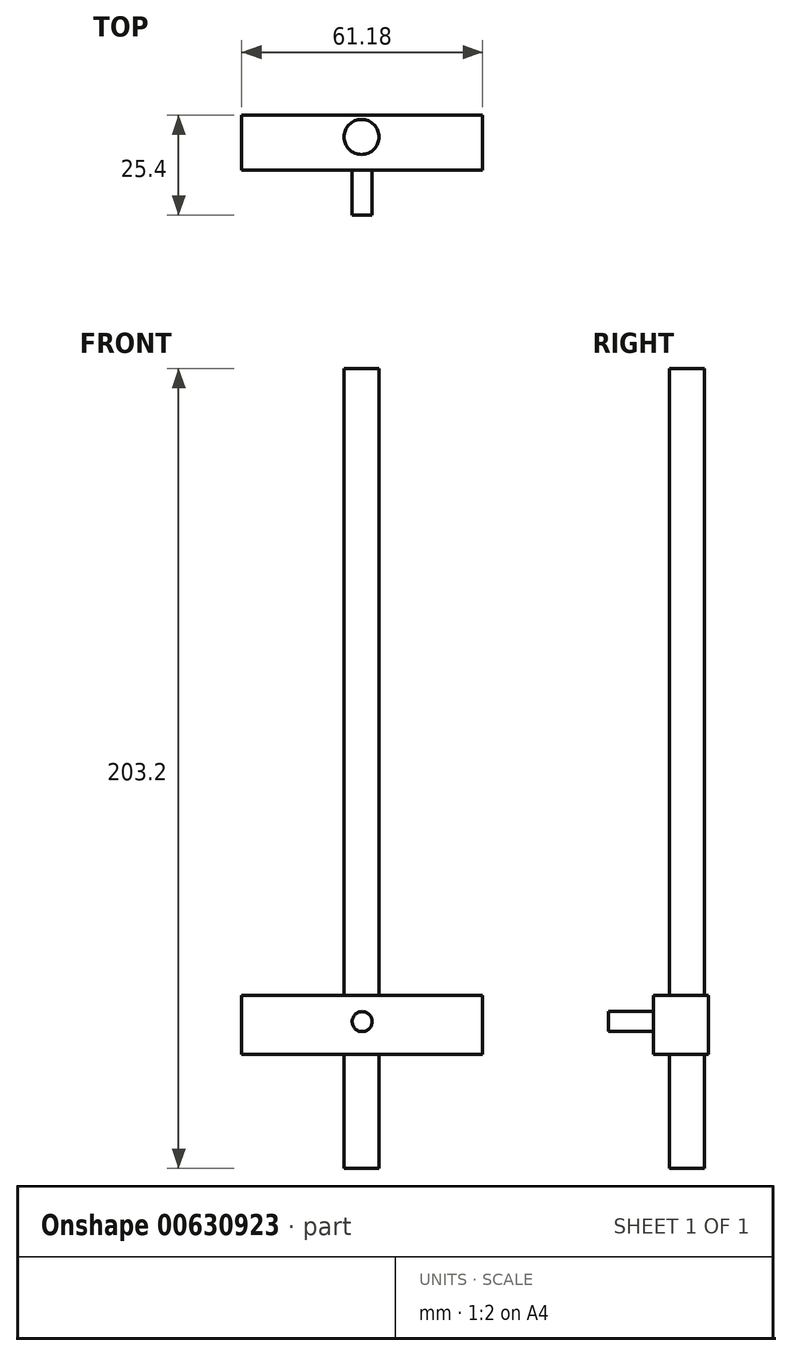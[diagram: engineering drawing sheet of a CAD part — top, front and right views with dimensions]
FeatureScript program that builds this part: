
annotation { "Feature Type Name" : "Feature", "Feature Type Description" : "" }
export const myFeature = defineFeature(function(context is Context, id is Id, definition is map)
    precondition{}
    {
        {
            var Q0;
            Q0=qCreatedBy(makeId("Top.planeOp"),FACE);
            var sketch = newSketch(context, id + "F0", { "sketchPlane" : qUnion([Q0])});
            skCircle(sketch, "E0", {"center": v(-34.22, 8.44) * mm, "radius": 4.45 * mm});
            skSolve(sketch);
        }
        {
            var Q0;
            Q0 = qSketchRegion(id + "F0", true);
            extrude(context, id + "F1", {"entities" : qUnion([Q0]), "oppositeDirection" : true, "depth" : 203.2 * mm, "offsetDistance" : 25.4 * mm});
        }
        {
            var Q0;
            Q0=qCreatedBy(makeId("Front.planeOp"),FACE);
            var sketch = newSketch(context, id + "F2", { "sketchPlane" : qUnion([Q0])});
            skLineSegment(sketch, "E1.bottom", {"start": v(-3.48, -159.3) * mm, "end": v(-64.66, -159.3) * mm});
            skLineSegment(sketch, "E1.top", {"start": v(-3.48, -174.25) * mm, "end": v(-64.66, -174.25) * mm});
            skLineSegment(sketch, "E1.left", {"start": v(-3.48, -159.3) * mm, "end": v(-3.48, -174.25) * mm});
            skLineSegment(sketch, "E1.right", {"start": v(-64.66, -159.3) * mm, "end": v(-64.66, -174.25) * mm});
            skCircle(sketch, "E2", {"center": v(-34.07, -165.91) * mm, "radius": 2.49 * mm});
            skPoint(sketch, "E2.centerSnap0", {"position": v(-34.07, -159.3) * mm});
            skSolve(sketch);
        }
        {
            var Q0;
            Q0 = qSketchRegion(id + "F2", true);
            extrude(context, id + "F3", {"entities" : qUnion([Q0]), "operationType" : NewBodyOperationType.ADD, "oppositeDirection" : true, "depth" : 13.97 * mm, "offsetDistance" : 25.4 * mm});
        }
        {
            var Q0;
            Q0=makeQuery(id+"F3.opExtrude","CAP_FACE",FACE,{"disambiguationData":[OSD([sQuery(id+"F2.wireOp",EDGE,"E1.bottom"),sQuery(id+"F2.wireOp",EDGE,"E1.top"),sQuery(id+"F2.wireOp",EDGE,"E1.left"),sQuery(id+"F2.wireOp",EDGE,"E1.right"),sQuery(id+"F2.wireOp",EDGE,"E2")])],"isStart":false});
            var sketch = newSketch(context, id + "F4", { "sketchPlane" : qUnion([Q0])});
            skCircle(sketch, "E3", {"center": v(34.07, -165.91) * mm, "radius": 2.54 * mm});
            skSolve(sketch);
        }
        {
            var Q0;
            Q0 = qSketchRegion(id + "F4", true);
            extrude(context, id + "F5", {"entities" : qUnion([Q0]), "operationType" : NewBodyOperationType.ADD, "oppositeDirection" : true, "depth" : 25.4 * mm, "offsetDistance" : 25.4 * mm});
        }
    });
